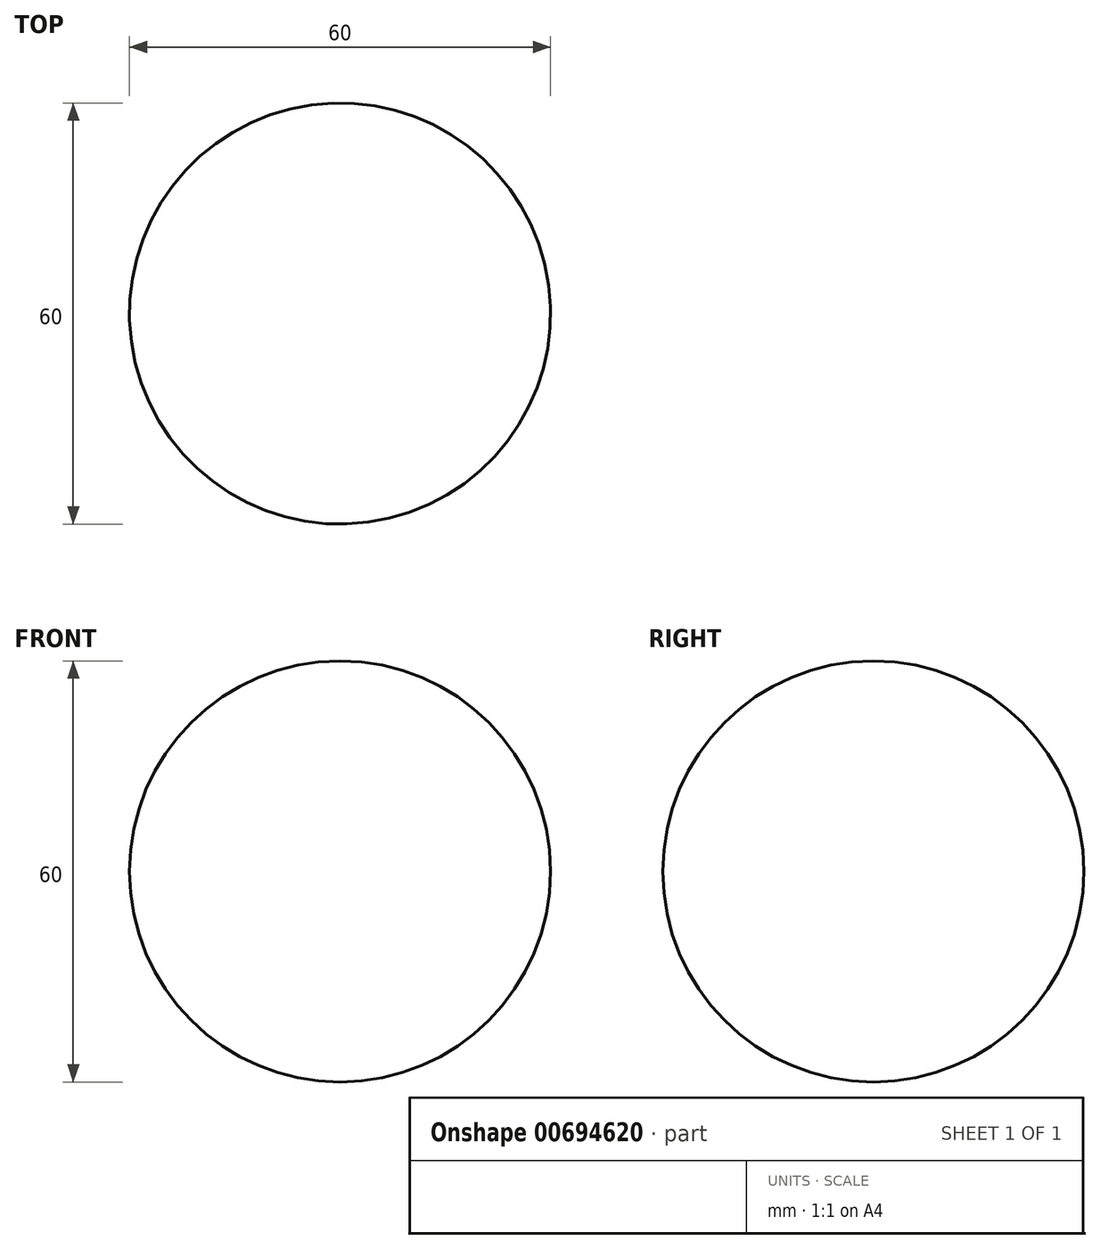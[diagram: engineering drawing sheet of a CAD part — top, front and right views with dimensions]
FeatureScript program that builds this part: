
annotation { "Feature Type Name" : "Feature", "Feature Type Description" : "" }
export const myFeature = defineFeature(function(context is Context, id is Id, definition is map)
    precondition{}
    {
        {
            var Q0;
            Q0=qCreatedBy(makeId("Top.planeOp"),FACE);
            var sketch = newSketch(context, id + "F0", { "sketchPlane" : qUnion([Q0])});
            skArc(sketch, "E0", {"start": v(29.73, 4.03) * mm, "mid": v(-4.03, 29.73) * mm, "end": v(-29.73, -4.03) * mm});
            skLineSegment(sketch, "E1", {"start": v(29.73, 4.03) * mm, "end": v(0, 0) * mm, "construction": true});
            skLineSegment(sketch, "E2", {"start": v(29.73, 4.03) * mm, "end": v(-29.73, -4.03) * mm, "construction": true});
            skLineSegment(sketch, "E3", {"start": v(29.73, 4.03) * mm, "end": v(-29.73, -4.03) * mm});
            skSolve(sketch);
        }
        {
            var Q0;
            Q0=makeQuery(id+"F0.imprint","IMPRINT",FACE,{"disambiguationData":[TD([[makeQuery(id+"F0.imprint","IMPRINT",EDGE,{"derivedFrom":sQuery(id+"F0.wireOp",EDGE,"E0")}),1.0]])]});
            var Q1;
            Q1=sQuery(id+"F0.wireOp",EDGE,"E3");
            revolve(context, id + "F1", {"entities" : qUnion([Q0]), "axis" : qUnion([Q1]), "revolveType" : RevolveType.FULL});
        }
    });
